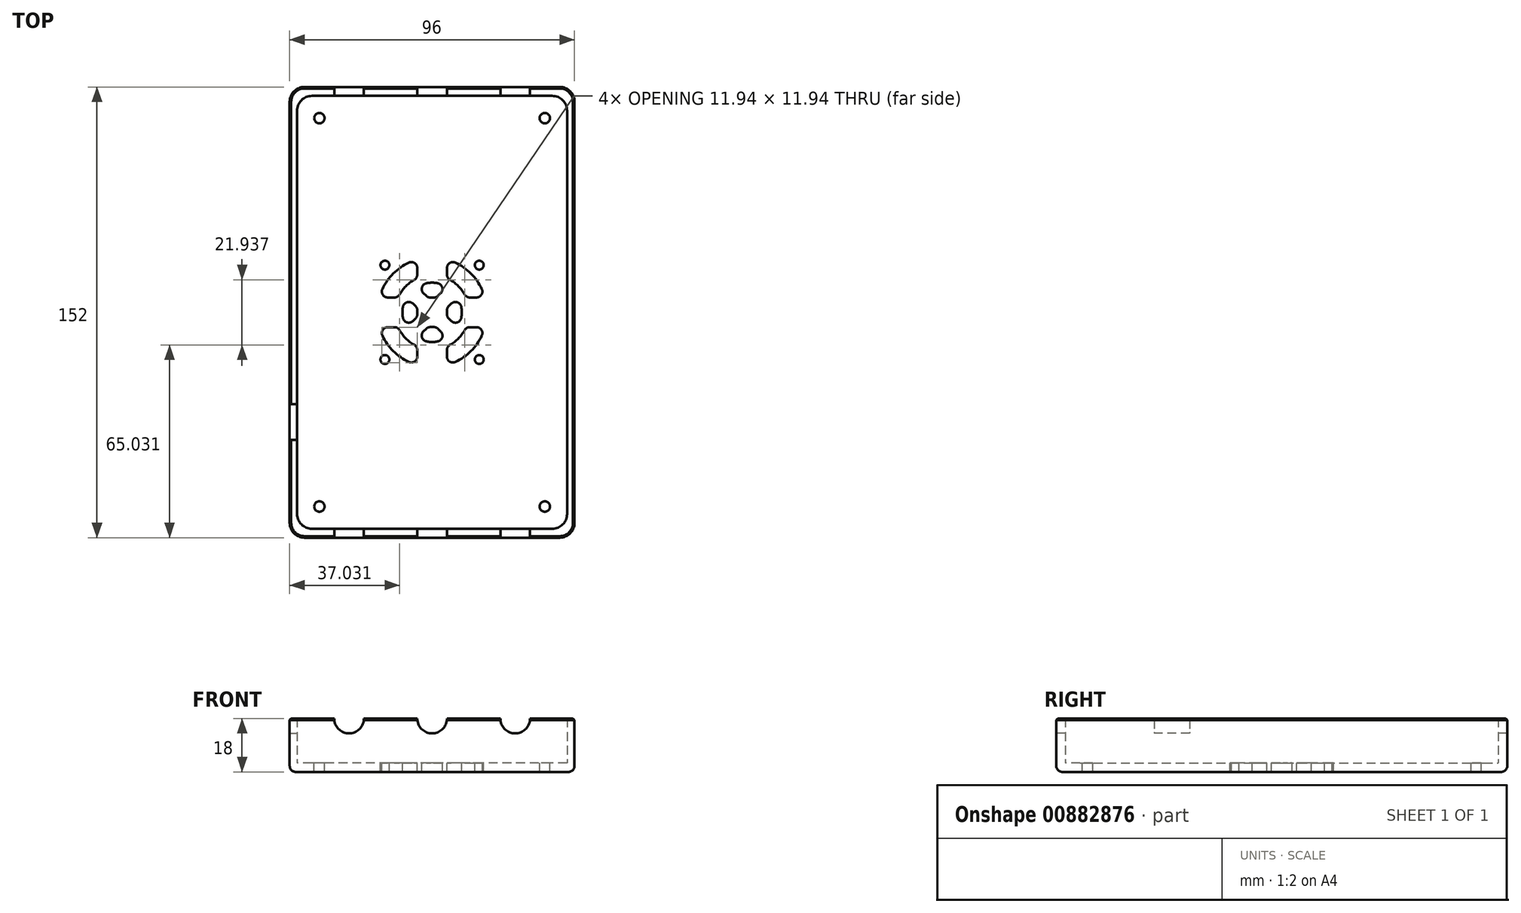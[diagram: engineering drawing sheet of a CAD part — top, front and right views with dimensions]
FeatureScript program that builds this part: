
annotation { "Feature Type Name" : "Feature", "Feature Type Description" : "" }
export const myFeature = defineFeature(function(context is Context, id is Id, definition is map)
    precondition{}
    {
        {
            var Q0;
            Q0=qCreatedBy(makeId("Top.planeOp"),FACE);
            var sketch = newSketch(context, id + "F0", { "sketchPlane" : qUnion([Q0])});
            skLineSegment(sketch, "E0.bottom", {"start": v(48, -76) * mm, "end": v(-48, -76) * mm});
            skLineSegment(sketch, "E0.top", {"start": v(48, 76) * mm, "end": v(-48, 76) * mm});
            skLineSegment(sketch, "E0.left", {"start": v(48, -76) * mm, "end": v(48, 76) * mm});
            skLineSegment(sketch, "E0.right", {"start": v(-48, -76) * mm, "end": v(-48, 76) * mm});
            skPoint(sketch, "E0.middle", {"position": v(0, 0) * mm});
            skSolve(sketch);
        }
        {
            var Q0;
            Q0=qSketchRegion(id+"F0",true);
            extrude(context, id + "F1", {"entities" : qUnion([Q0]), "depth" : 3 * mm, "offsetDistance" : 25 * mm});
        }
        {
            var Q0;
            Q0=makeQuery(id+"F1.opExtrude","CAP_FACE",FACE,{"disambiguationData":[OSD([sQuery(id+"F0.wireOp",EDGE,"E0.bottom"),sQuery(id+"F0.wireOp",EDGE,"E0.top"),sQuery(id+"F0.wireOp",EDGE,"E0.left"),sQuery(id+"F0.wireOp",EDGE,"E0.right")])],"isStart":false});
            var sketch = newSketch(context, id + "F2", { "sketchPlane" : qUnion([Q0])});
            skLineSegment(sketch, "E1.bottom", {"start": v(48, -76) * mm, "end": v(-48, -76) * mm});
            skLineSegment(sketch, "E1.top", {"start": v(48, 76) * mm, "end": v(-48, 76) * mm});
            skLineSegment(sketch, "E1.left", {"start": v(48, -76) * mm, "end": v(48, 76) * mm});
            skLineSegment(sketch, "E1.right", {"start": v(-48, -76) * mm, "end": v(-48, 76) * mm});
            skPoint(sketch, "E1.middle", {"position": v(0, 0) * mm});
            skLineSegment(sketch, "E2.bottom", {"start": v(45.5, -73) * mm, "end": v(-45.5, -73) * mm});
            skLineSegment(sketch, "E2.top", {"start": v(45.5, 73) * mm, "end": v(-45.5, 73) * mm});
            skLineSegment(sketch, "E2.left", {"start": v(45.5, -73) * mm, "end": v(45.5, 73) * mm});
            skLineSegment(sketch, "E2.right", {"start": v(-45.5, -73) * mm, "end": v(-45.5, 73) * mm});
            skSolve(sketch);
        }
        {
            var Q0;
            Q0=qSketchRegion(id+"F2",true);
            extrude(context, id + "F3", {"entities" : qUnion([Q0]), "operationType" : NewBodyOperationType.ADD, "depth" : 15 * mm, "offsetDistance" : 25 * mm});
        }
        {
            var Q0;
            Q0=makeQuery(id+"F1.opExtrude","CAP_FACE",FACE,{"disambiguationData":[OSD([sQuery(id+"F0.wireOp",EDGE,"E0.bottom"),sQuery(id+"F0.wireOp",EDGE,"E0.top"),sQuery(id+"F0.wireOp",EDGE,"E0.left"),sQuery(id+"F0.wireOp",EDGE,"E0.right")])],"isStart":false});
            var sketch = newSketch(context, id + "F4", { "sketchPlane" : qUnion([Q0])});
            skCircle(sketch, "E3", {"center": v(-38, 65.5) * mm, "radius": 1.75 * mm});
            skCircle(sketch, "E4.MirrorC", {"center": v(38, 65.5) * mm, "radius": 1.75 * mm});
            skCircle(sketch, "E5.MirrorC", {"center": v(-38, -65.5) * mm, "radius": 1.75 * mm});
            skCircle(sketch, "E6.MirrorC", {"center": v(38, -65.5) * mm, "radius": 1.75 * mm});
            skSolve(sketch);
        }
        {
            var Q0;
            Q0=qSketchRegion(id+"F4",true);
            extrude(context, id + "F5", {"entities" : qUnion([Q0]), "operationType" : NewBodyOperationType.REMOVE, "endBound" : BoundingType.UP_TO_NEXT, "oppositeDirection" : true, "depth" : 25 * mm, "offsetDistance" : 25 * mm});
        }
        {
            var Q0;
            Q0=makeQuery(id+"F3.boolean.opBoolean","MERGE",EDGE,{"derivedFrom":[makeQuery(id+"F1.opExtrude","SWEPT_EDGE",EDGE,{"disambiguationData":[OSD([sQuery(id+"F0.wireOp",EDGE,"E0.bottom"),sQuery(id+"F0.wireOp",EDGE,"E0.right")])]}),makeQuery(id+"F3.opExtrude","SWEPT_EDGE",EDGE,{"disambiguationData":[OSD([sQuery(id+"F2.wireOp",EDGE,"E1.bottom"),sQuery(id+"F2.wireOp",EDGE,"E1.right")])]})]});
            var Q1;
            Q1=makeQuery(id+"F3.boolean.opBoolean","MERGE",EDGE,{"derivedFrom":[makeQuery(id+"F1.opExtrude","SWEPT_EDGE",EDGE,{"disambiguationData":[OSD([sQuery(id+"F0.wireOp",EDGE,"E0.bottom"),sQuery(id+"F0.wireOp",EDGE,"E0.left")])]}),makeQuery(id+"F3.opExtrude","SWEPT_EDGE",EDGE,{"disambiguationData":[OSD([sQuery(id+"F2.wireOp",EDGE,"E1.bottom"),sQuery(id+"F2.wireOp",EDGE,"E1.left")])]})]});
            var Q2;
            Q2=makeQuery(id+"F3.opExtrude","SWEPT_EDGE",EDGE,{"disambiguationData":[OSD([sQuery(id+"F2.wireOp",EDGE,"E2.bottom"),sQuery(id+"F2.wireOp",EDGE,"E2.left")])]});
            var Q3;
            Q3=makeQuery(id+"F3.opExtrude","SWEPT_EDGE",EDGE,{"disambiguationData":[OSD([sQuery(id+"F2.wireOp",EDGE,"E2.bottom"),sQuery(id+"F2.wireOp",EDGE,"E2.right")])]});
            var Q4;
            Q4=makeQuery(id+"F3.boolean.opBoolean","MERGE",EDGE,{"derivedFrom":[makeQuery(id+"F1.opExtrude","SWEPT_EDGE",EDGE,{"disambiguationData":[OSD([sQuery(id+"F0.wireOp",EDGE,"E0.top"),sQuery(id+"F0.wireOp",EDGE,"E0.right")])]}),makeQuery(id+"F3.opExtrude","SWEPT_EDGE",EDGE,{"disambiguationData":[OSD([sQuery(id+"F2.wireOp",EDGE,"E1.top"),sQuery(id+"F2.wireOp",EDGE,"E1.right")])]})]});
            var Q5;
            Q5=makeQuery(id+"F3.opExtrude","SWEPT_EDGE",EDGE,{"disambiguationData":[OSD([sQuery(id+"F2.wireOp",EDGE,"E2.top"),sQuery(id+"F2.wireOp",EDGE,"E2.right")])]});
            var Q6;
            Q6=makeQuery(id+"F3.boolean.opBoolean","MERGE",EDGE,{"derivedFrom":[makeQuery(id+"F1.opExtrude","SWEPT_EDGE",EDGE,{"disambiguationData":[OSD([sQuery(id+"F0.wireOp",EDGE,"E0.top"),sQuery(id+"F0.wireOp",EDGE,"E0.left")])]}),makeQuery(id+"F3.opExtrude","SWEPT_EDGE",EDGE,{"disambiguationData":[OSD([sQuery(id+"F2.wireOp",EDGE,"E1.top"),sQuery(id+"F2.wireOp",EDGE,"E1.left")])]})]});
            var Q7;
            Q7=makeQuery(id+"F3.opExtrude","SWEPT_EDGE",EDGE,{"disambiguationData":[OSD([sQuery(id+"F2.wireOp",EDGE,"E2.top"),sQuery(id+"F2.wireOp",EDGE,"E2.left")])]});
            fillet(context, id + "F6", {"entities" : qUnion([Q0, Q1, Q2, Q3, Q4, Q5, Q6, Q7]), "radius" : 5 * mm, "tangentPropagation" : true, "allowEdgeOverflow" : false});
        }
        {
            var Q0;
            Q0=makeQuery(id+"F1.opExtrude","CAP_EDGE",EDGE,{"disambiguationData":[OSD([sQuery(id+"F0.wireOp",EDGE,"E0.right")])],"isStart":true});
            fillet(context, id + "F7", {"entities" : qUnion([Q0]), "radius" : 2 * mm, "tangentPropagation" : true, "allowEdgeOverflow" : false});
        }
        {
            var Q0;
            Q0=makeQuery(id+"F3.boolean.opBoolean","MERGE",FACE,{"derivedFrom":[makeQuery(id+"F1.opExtrude","SWEPT_FACE",FACE,{"disambiguationData":[OSD([sQuery(id+"F0.wireOp",EDGE,"E0.bottom")])]}),makeQuery(id+"F3.opExtrude","SWEPT_FACE",FACE,{"disambiguationData":[OSD([sQuery(id+"F2.wireOp",EDGE,"E1.bottom")])]})]});
            var sketch = newSketch(context, id + "F8", { "sketchPlane" : qUnion([Q0])});
            skCircle(sketch, "E7", {"center": v(-28, 18) * mm, "radius": 5 * mm});
            skCircle(sketch, "E8", {"center": v(0, 18) * mm, "radius": 5 * mm});
            skCircle(sketch, "E9", {"center": v(28, 18) * mm, "radius": 5 * mm});
            skSolve(sketch);
        }
        {
            var Q0;
            Q0=qSketchRegion(id+"F8",true);
            extrude(context, id + "F9", {"entities" : qUnion([Q0]), "operationType" : NewBodyOperationType.REMOVE, "endBound" : BoundingType.THROUGH_ALL, "oppositeDirection" : true, "depth" : 25 * mm, "offsetDistance" : 25 * mm});
        }
        {
            var Q0;
            Q0=makeQuery(id+"F3.opExtrude","SWEPT_FACE",FACE,{"disambiguationData":[OSD([sQuery(id+"F2.wireOp",EDGE,"E2.left")])]});
            var sketch = newSketch(context, id + "F10", { "sketchPlane" : qUnion([Q0])});
            skLineSegment(sketch, "E10.bottom", {"start": v(43, 13) * mm, "end": v(31, 13) * mm});
            skLineSegment(sketch, "E10.top", {"start": v(43, 33.9) * mm, "end": v(31, 33.9) * mm});
            skLineSegment(sketch, "E10.left", {"start": v(43, 13) * mm, "end": v(43, 33.9) * mm});
            skLineSegment(sketch, "E10.right", {"start": v(31, 13) * mm, "end": v(31, 33.9) * mm});
            skSolve(sketch);
        }
        {
            var Q0;
            Q0=qSketchRegion(id+"F10",true);
            extrude(context, id + "F11", {"entities" : qUnion([Q0]), "operationType" : NewBodyOperationType.REMOVE, "endBound" : BoundingType.THROUGH_ALL, "depth" : 25 * mm, "offsetDistance" : 25 * mm});
        }
        {
            var Q0;
            Q0=makeQuery(id+"F1.opExtrude","CAP_FACE",FACE,{"disambiguationData":[OSD([sQuery(id+"F0.wireOp",EDGE,"E0.bottom"),sQuery(id+"F0.wireOp",EDGE,"E0.top"),sQuery(id+"F0.wireOp",EDGE,"E0.left"),sQuery(id+"F0.wireOp",EDGE,"E0.right")])],"isStart":false});
            var sketch = newSketch(context, id + "F12", { "sketchPlane" : qUnion([Q0])});
            skLineSegment(sketch, "E11", {"start": v(-18.16, -18.16) * mm, "end": v(29.37, 29.37) * mm, "construction": true});
            skLineSegment(sketch, "E12", {"start": v(19.53, -19.53) * mm, "end": v(-26.87, 26.87) * mm, "construction": true});
            skCircle(sketch, "E13", {"center": v(-15.9, -15.9) * mm, "radius": 1.5 * mm});
            skCircle(sketch, "E14.1.0", {"center": v(15.9, -15.9) * mm, "radius": 1.5 * mm});
            skCircle(sketch, "E14.2.0", {"center": v(15.9, 15.9) * mm, "radius": 1.5 * mm});
            skCircle(sketch, "E14.3.0", {"center": v(-15.9, 15.9) * mm, "radius": 1.5 * mm});
            skPoint(sketch, "E14.center", {"position": v(0, 0) * mm});
            skArc(sketch, "E15", {"start": v(16.75, 7.85) * mm, "mid": v(13.08, 13.08) * mm, "end": v(7.85, 16.75) * mm});
            skArc(sketch, "E16", {"start": v(10.95, 6.03) * mm, "mid": v(8.84, 8.84) * mm, "end": v(6.03, 10.95) * mm});
            skLineSegment(sketch, "E17", {"start": v(12.7, 5) * mm, "end": v(14.94, 5) * mm});
            skLineSegment(sketch, "E18.MirrorCS", {"start": v(12.7, -5) * mm, "end": v(14.94, -5) * mm});
            skPoint(sketch, "E19.orphan", {"position": v(28.67, -5) * mm});
            skPoint(sketch, "E20.orphan", {"position": v(8.36, 5) * mm});
            skPoint(sketch, "E21.orphan", {"position": v(8.36, -5) * mm});
            skPoint(sketch, "E22.orphan", {"position": v(28.67, 5) * mm});
            skPoint(sketch, "E23.visualSharp", {"position": v(11.46, -5) * mm});
            skArc(sketch, "E23.filletArc", {"start": v(12.7, -5) * mm, "mid": v(11.68, -5.28) * mm, "end": v(10.95, -6.03) * mm});
            skPoint(sketch, "E24.visualSharp", {"position": v(17.81, -5) * mm});
            skArc(sketch, "E24.filletArc", {"start": v(16.75, -7.85) * mm, "mid": v(16.63, -5.93) * mm, "end": v(14.94, -5) * mm});
            skPoint(sketch, "E25.visualSharp", {"position": v(11.46, 5) * mm});
            skArc(sketch, "E25.filletArc", {"start": v(10.95, 6.03) * mm, "mid": v(11.68, 5.28) * mm, "end": v(12.7, 5) * mm});
            skPoint(sketch, "E26.visualSharp", {"position": v(17.81, 5) * mm});
            skArc(sketch, "E26.filletArc", {"start": v(14.94, 5) * mm, "mid": v(16.63, 5.93) * mm, "end": v(16.75, 7.85) * mm});
            skArc(sketch, "E27.1.0", {"start": v(7.85, 16.75) * mm, "mid": v(5.93, 16.63) * mm, "end": v(5, 14.94) * mm});
            skLineSegment(sketch, "E27.1.1", {"start": v(5, 12.7) * mm, "end": v(5, 14.94) * mm});
            skArc(sketch, "E27.1.2", {"start": v(5, 12.7) * mm, "mid": v(5.28, 11.68) * mm, "end": v(6.03, 10.95) * mm});
            skArc(sketch, "E27.1.3", {"start": v(-6.03, 10.95) * mm, "mid": v(-5.28, 11.68) * mm, "end": v(-5, 12.7) * mm});
            skLineSegment(sketch, "E27.1.4", {"start": v(-5, 12.7) * mm, "end": v(-5, 14.94) * mm});
            skArc(sketch, "E27.1.5", {"start": v(-5, 14.94) * mm, "mid": v(-5.93, 16.63) * mm, "end": v(-7.85, 16.75) * mm});
            skArc(sketch, "E27.2.0", {"start": v(-16.75, 7.85) * mm, "mid": v(-16.63, 5.93) * mm, "end": v(-14.94, 5) * mm});
            skLineSegment(sketch, "E27.2.1", {"start": v(-12.7, 5) * mm, "end": v(-14.94, 5) * mm});
            skArc(sketch, "E27.2.2", {"start": v(-12.7, 5) * mm, "mid": v(-11.68, 5.28) * mm, "end": v(-10.95, 6.03) * mm});
            skArc(sketch, "E27.2.3", {"start": v(-10.95, -6.03) * mm, "mid": v(-11.68, -5.28) * mm, "end": v(-12.7, -5) * mm});
            skLineSegment(sketch, "E27.2.4", {"start": v(-12.7, -5) * mm, "end": v(-14.94, -5) * mm});
            skArc(sketch, "E27.2.5", {"start": v(-14.94, -5) * mm, "mid": v(-16.63, -5.93) * mm, "end": v(-16.75, -7.85) * mm});
            skArc(sketch, "E27.3.0", {"start": v(-7.85, -16.75) * mm, "mid": v(-5.93, -16.63) * mm, "end": v(-5, -14.94) * mm});
            skLineSegment(sketch, "E27.3.1", {"start": v(-5, -12.7) * mm, "end": v(-5, -14.94) * mm});
            skArc(sketch, "E27.3.2", {"start": v(-5, -12.7) * mm, "mid": v(-5.28, -11.68) * mm, "end": v(-6.03, -10.95) * mm});
            skArc(sketch, "E27.3.3", {"start": v(6.03, -10.95) * mm, "mid": v(5.28, -11.68) * mm, "end": v(5, -12.7) * mm});
            skLineSegment(sketch, "E27.3.4", {"start": v(5, -12.7) * mm, "end": v(5, -14.94) * mm});
            skArc(sketch, "E27.3.5", {"start": v(5, -14.94) * mm, "mid": v(5.93, -16.63) * mm, "end": v(7.85, -16.75) * mm});
            skArc(sketch, "E28.trimOffspring", {"start": v(-7.85, 16.75) * mm, "mid": v(-13.08, 13.08) * mm, "end": v(-16.75, 7.85) * mm});
            skArc(sketch, "E29.trimOffspring", {"start": v(-6.03, 10.95) * mm, "mid": v(-8.84, 8.84) * mm, "end": v(-10.95, 6.03) * mm});
            skArc(sketch, "E30.trimOffspring", {"start": v(-10.95, -6.03) * mm, "mid": v(-8.84, -8.84) * mm, "end": v(-6.03, -10.95) * mm});
            skArc(sketch, "E31.trimOffspring", {"start": v(-16.75, -7.85) * mm, "mid": v(-13.08, -13.08) * mm, "end": v(-7.85, -16.75) * mm});
            skArc(sketch, "E32.trimOffspring", {"start": v(6.03, -10.95) * mm, "mid": v(8.84, -8.84) * mm, "end": v(10.95, -6.03) * mm});
            skArc(sketch, "E33.trimOffspring", {"start": v(7.85, -16.75) * mm, "mid": v(13.08, -13.08) * mm, "end": v(16.75, -7.85) * mm});
            skArc(sketch, "E34", {"start": v(9.82, -1.87) * mm, "mid": v(10, 0) * mm, "end": v(9.82, 1.87) * mm});
            skArc(sketch, "E35", {"start": v(4.98, -0.44) * mm, "mid": v(5, 0) * mm, "end": v(4.98, 0.44) * mm});
            skLineSegment(sketch, "E36", {"start": v(2.02, -5.56) * mm, "end": v(2.9, -6.44) * mm});
            skLineSegment(sketch, "E37.MirrorCS", {"start": v(5.56, -2.02) * mm, "end": v(6.44, -2.9) * mm});
            skPoint(sketch, "E38.orphan", {"position": v(9.7, -6.17) * mm});
            skPoint(sketch, "E39.orphan", {"position": v(6.17, -9.7) * mm});
            skPoint(sketch, "E40.orphan", {"position": v(0.7, -4.24) * mm});
            skPoint(sketch, "E41.orphan", {"position": v(4.24, -0.7) * mm});
            skPoint(sketch, "E42.visualSharp", {"position": v(1.3, -4.83) * mm});
            skArc(sketch, "E42.filletArc", {"start": v(2.02, -5.56) * mm, "mid": v(1.3, -5.1) * mm, "end": v(0.44, -4.98) * mm});
            skPoint(sketch, "E43.visualSharp", {"position": v(5.08, -8.61) * mm});
            skArc(sketch, "E43.filletArc", {"start": v(1.87, -9.82) * mm, "mid": v(3.4, -8.45) * mm, "end": v(2.9, -6.44) * mm});
            skPoint(sketch, "E44.visualSharp", {"position": v(4.83, -1.3) * mm});
            skArc(sketch, "E44.filletArc", {"start": v(4.98, -0.44) * mm, "mid": v(5.1, -1.3) * mm, "end": v(5.56, -2.02) * mm});
            skPoint(sketch, "E45.visualSharp", {"position": v(8.61, -5.08) * mm});
            skArc(sketch, "E45.filletArc", {"start": v(6.44, -2.9) * mm, "mid": v(8.45, -3.4) * mm, "end": v(9.82, -1.87) * mm});
            skArc(sketch, "E46.1.0", {"start": v(5.56, 2.02) * mm, "mid": v(5.1, 1.3) * mm, "end": v(4.98, 0.44) * mm});
            skLineSegment(sketch, "E46.1.1", {"start": v(5.56, 2.02) * mm, "end": v(6.44, 2.9) * mm});
            skArc(sketch, "E46.1.2", {"start": v(9.82, 1.87) * mm, "mid": v(8.45, 3.4) * mm, "end": v(6.44, 2.9) * mm});
            skArc(sketch, "E46.1.3", {"start": v(0.44, 4.98) * mm, "mid": v(1.3, 5.1) * mm, "end": v(2.02, 5.56) * mm});
            skLineSegment(sketch, "E46.1.4", {"start": v(2.02, 5.56) * mm, "end": v(2.9, 6.44) * mm});
            skArc(sketch, "E46.1.5", {"start": v(2.9, 6.44) * mm, "mid": v(3.4, 8.45) * mm, "end": v(1.87, 9.82) * mm});
            skArc(sketch, "E46.2.0", {"start": v(-2.02, 5.56) * mm, "mid": v(-1.3, 5.1) * mm, "end": v(-0.44, 4.98) * mm});
            skLineSegment(sketch, "E46.2.1", {"start": v(-2.02, 5.56) * mm, "end": v(-2.9, 6.44) * mm});
            skArc(sketch, "E46.2.2", {"start": v(-1.87, 9.82) * mm, "mid": v(-3.4, 8.45) * mm, "end": v(-2.9, 6.44) * mm});
            skArc(sketch, "E46.2.3", {"start": v(-4.98, 0.44) * mm, "mid": v(-5.1, 1.3) * mm, "end": v(-5.56, 2.02) * mm});
            skLineSegment(sketch, "E46.2.4", {"start": v(-5.56, 2.02) * mm, "end": v(-6.44, 2.9) * mm});
            skArc(sketch, "E46.2.5", {"start": v(-6.44, 2.9) * mm, "mid": v(-8.45, 3.4) * mm, "end": v(-9.82, 1.87) * mm});
            skArc(sketch, "E46.3.0", {"start": v(-5.56, -2.02) * mm, "mid": v(-5.1, -1.3) * mm, "end": v(-4.98, -0.44) * mm});
            skLineSegment(sketch, "E46.3.1", {"start": v(-5.56, -2.02) * mm, "end": v(-6.44, -2.9) * mm});
            skArc(sketch, "E46.3.2", {"start": v(-9.82, -1.87) * mm, "mid": v(-8.45, -3.4) * mm, "end": v(-6.44, -2.9) * mm});
            skArc(sketch, "E46.3.3", {"start": v(-0.44, -4.98) * mm, "mid": v(-1.3, -5.1) * mm, "end": v(-2.02, -5.56) * mm});
            skLineSegment(sketch, "E46.3.4", {"start": v(-2.02, -5.56) * mm, "end": v(-2.9, -6.44) * mm});
            skArc(sketch, "E46.3.5", {"start": v(-2.9, -6.44) * mm, "mid": v(-3.4, -8.45) * mm, "end": v(-1.87, -9.82) * mm});
            skArc(sketch, "E47.trimOffspring", {"start": v(0.44, 4.98) * mm, "mid": v(0, 5) * mm, "end": v(-0.44, 4.98) * mm});
            skArc(sketch, "E48.trimOffspring", {"start": v(-4.98, 0.44) * mm, "mid": v(-5, 0) * mm, "end": v(-4.98, -0.44) * mm});
            skArc(sketch, "E49.trimOffspring", {"start": v(-0.44, -4.98) * mm, "mid": v(0, -5) * mm, "end": v(0.44, -4.98) * mm});
            skArc(sketch, "E50.trimOffspring", {"start": v(1.87, 9.82) * mm, "mid": v(0, 10) * mm, "end": v(-1.87, 9.82) * mm});
            skArc(sketch, "E51.trimOffspring", {"start": v(-9.82, 1.87) * mm, "mid": v(-10, 0) * mm, "end": v(-9.82, -1.87) * mm});
            skArc(sketch, "E52.trimOffspring", {"start": v(-1.87, -9.82) * mm, "mid": v(0, -10) * mm, "end": v(1.87, -9.82) * mm});
            skSolve(sketch);
        }
        {
            var Q0;
            Q0 = qSketchRegion(id + "F12", true);
            extrude(context, id + "F13", {"entities" : qUnion([Q0]), "operationType" : NewBodyOperationType.REMOVE, "endBound" : BoundingType.UP_TO_NEXT, "oppositeDirection" : true, "depth" : 25 * mm, "offsetDistance" : 25 * mm});
        }
        {
            var Q0;
            Q0=makeQuery(id+"F3.opExtrude","CAP_EDGE",EDGE,{"disambiguationData":[OSD([sQuery(id+"F2.wireOp",EDGE,"E1.left")])],"isStart":false});
            var Q1;
            {var subQ0=sQuery(id+"F2.wireOp",EDGE,"E1.top");Q1=makeQuery(id+"F9.boolean.opBoolean","SPLIT",EDGE,{"disambiguationData":[TD([makeQuery(id+"F1.opExtrude","SWEPT_FACE",FACE,{"disambiguationData":[OSD([sQuery(id+"F0.wireOp",EDGE,"E0.top")])]}),makeQuery(id+"F3.opExtrude","CAP_FACE",FACE,{"disambiguationData":[OSD([sQuery(id+"F2.wireOp",EDGE,"E1.bottom"),subQ0,sQuery(id+"F2.wireOp",EDGE,"E1.left"),sQuery(id+"F2.wireOp",EDGE,"E1.right"),sQuery(id+"F2.wireOp",EDGE,"E2.bottom"),sQuery(id+"F2.wireOp",EDGE,"E2.top"),sQuery(id+"F2.wireOp",EDGE,"E2.left"),sQuery(id+"F2.wireOp",EDGE,"E2.right")])],"isStart":false}),makeQuery(id+"F3.opExtrude","SWEPT_FACE",FACE,{"disambiguationData":[OSD([subQ0])]}),makeQuery(id+"F9.opExtrude","SWEPT_FACE",FACE,{"disambiguationData":[OSD([sQuery(id+"F8.wireOp",EDGE,"E8")])]}),makeQuery(id+"F9.opExtrude","SWEPT_FACE",FACE,{"disambiguationData":[OSD([sQuery(id+"F8.wireOp",EDGE,"E9")])]})])],"derivedFrom":makeQuery(id+"F3.opExtrude","CAP_EDGE",EDGE,{"disambiguationData":[OSD([subQ0])],"isStart":false})});}
            var Q2;
            {var subQ0=sQuery(id+"F2.wireOp",EDGE,"E1.top");Q2=makeQuery(id+"F9.boolean.opBoolean","SPLIT",EDGE,{"disambiguationData":[TD([makeQuery(id+"F1.opExtrude","SWEPT_FACE",FACE,{"disambiguationData":[OSD([sQuery(id+"F0.wireOp",EDGE,"E0.top")])]}),makeQuery(id+"F3.opExtrude","CAP_FACE",FACE,{"disambiguationData":[OSD([sQuery(id+"F2.wireOp",EDGE,"E1.bottom"),subQ0,sQuery(id+"F2.wireOp",EDGE,"E1.left"),sQuery(id+"F2.wireOp",EDGE,"E1.right"),sQuery(id+"F2.wireOp",EDGE,"E2.bottom"),sQuery(id+"F2.wireOp",EDGE,"E2.top"),sQuery(id+"F2.wireOp",EDGE,"E2.left"),sQuery(id+"F2.wireOp",EDGE,"E2.right")])],"isStart":false}),makeQuery(id+"F3.opExtrude","SWEPT_FACE",FACE,{"disambiguationData":[OSD([subQ0])]}),makeQuery(id+"F9.opExtrude","SWEPT_FACE",FACE,{"disambiguationData":[OSD([sQuery(id+"F8.wireOp",EDGE,"E7")])]}),makeQuery(id+"F9.opExtrude","SWEPT_FACE",FACE,{"disambiguationData":[OSD([sQuery(id+"F8.wireOp",EDGE,"E8")])]})])],"derivedFrom":makeQuery(id+"F3.opExtrude","CAP_EDGE",EDGE,{"disambiguationData":[OSD([subQ0])],"isStart":false})});}
            var Q3;
            {var subQ0=sQuery(id+"F2.wireOp",EDGE,"E1.right");var subQ1=sQuery(id+"F2.wireOp",EDGE,"E1.top");var subQ2=sQuery(id+"F0.wireOp",EDGE,"E0.top");Q3=makeQuery(id+"F9.boolean.opBoolean","SPLIT",EDGE,{"disambiguationData":[TD([makeQuery(id+"F1.opExtrude","SWEPT_FACE",FACE,{"disambiguationData":[OSD([subQ2])]}),makeQuery(id+"F3.opExtrude","CAP_FACE",FACE,{"disambiguationData":[OSD([sQuery(id+"F2.wireOp",EDGE,"E1.bottom"),subQ1,sQuery(id+"F2.wireOp",EDGE,"E1.left"),subQ0,sQuery(id+"F2.wireOp",EDGE,"E2.bottom"),sQuery(id+"F2.wireOp",EDGE,"E2.top"),sQuery(id+"F2.wireOp",EDGE,"E2.left"),sQuery(id+"F2.wireOp",EDGE,"E2.right")])],"isStart":false}),makeQuery(id+"F3.opExtrude","SWEPT_FACE",FACE,{"disambiguationData":[OSD([subQ1])]}),makeQuery(id+"F6.opFillet","BLEND_FACE",FACE,{"disambiguationData":[OSD([subQ2,sQuery(id+"F0.wireOp",EDGE,"E0.right"),subQ1,subQ0])]}),makeQuery(id+"F9.opExtrude","SWEPT_FACE",FACE,{"disambiguationData":[OSD([sQuery(id+"F8.wireOp",EDGE,"E7")])]})])],"derivedFrom":makeQuery(id+"F3.opExtrude","CAP_EDGE",EDGE,{"disambiguationData":[OSD([subQ1])],"isStart":false})});}
            var Q4;
            {var subQ0=sQuery(id+"F2.wireOp",EDGE,"E1.right");Q4=makeQuery(id+"F11.boolean.opBoolean","SPLIT",EDGE,{"disambiguationData":[TD([makeQuery(id+"F11.opExtrude","SWEPT_FACE",FACE,{"disambiguationData":[OSD([sQuery(id+"F10.wireOp",EDGE,"E10.left")])]})])],"derivedFrom":makeQuery(id+"F3.opExtrude","CAP_EDGE",EDGE,{"disambiguationData":[OSD([subQ0])],"isStart":false})});}
            var Q5;
            {var subQ0=sQuery(id+"F2.wireOp",EDGE,"E1.bottom");Q5=makeQuery(id+"F9.boolean.opBoolean","SPLIT",EDGE,{"disambiguationData":[TD([makeQuery(id+"F1.opExtrude","SWEPT_FACE",FACE,{"disambiguationData":[OSD([sQuery(id+"F0.wireOp",EDGE,"E0.bottom")])]}),makeQuery(id+"F3.opExtrude","SWEPT_FACE",FACE,{"disambiguationData":[OSD([subQ0])]}),makeQuery(id+"F3.opExtrude","CAP_FACE",FACE,{"disambiguationData":[OSD([subQ0,sQuery(id+"F2.wireOp",EDGE,"E1.top"),sQuery(id+"F2.wireOp",EDGE,"E1.left"),sQuery(id+"F2.wireOp",EDGE,"E1.right"),sQuery(id+"F2.wireOp",EDGE,"E2.bottom"),sQuery(id+"F2.wireOp",EDGE,"E2.top"),sQuery(id+"F2.wireOp",EDGE,"E2.left"),sQuery(id+"F2.wireOp",EDGE,"E2.right")])],"isStart":false}),makeQuery(id+"F9.opExtrude","SWEPT_FACE",FACE,{"disambiguationData":[OSD([sQuery(id+"F8.wireOp",EDGE,"E7")])]}),makeQuery(id+"F9.opExtrude","SWEPT_FACE",FACE,{"disambiguationData":[OSD([sQuery(id+"F8.wireOp",EDGE,"E8")])]})])],"derivedFrom":makeQuery(id+"F3.opExtrude","CAP_EDGE",EDGE,{"disambiguationData":[OSD([subQ0])],"isStart":false})});}
            var Q6;
            {var subQ0=sQuery(id+"F2.wireOp",EDGE,"E1.bottom");Q6=makeQuery(id+"F9.boolean.opBoolean","SPLIT",EDGE,{"disambiguationData":[TD([makeQuery(id+"F1.opExtrude","SWEPT_FACE",FACE,{"disambiguationData":[OSD([sQuery(id+"F0.wireOp",EDGE,"E0.bottom")])]}),makeQuery(id+"F3.opExtrude","SWEPT_FACE",FACE,{"disambiguationData":[OSD([subQ0])]}),makeQuery(id+"F3.opExtrude","CAP_FACE",FACE,{"disambiguationData":[OSD([subQ0,sQuery(id+"F2.wireOp",EDGE,"E1.top"),sQuery(id+"F2.wireOp",EDGE,"E1.left"),sQuery(id+"F2.wireOp",EDGE,"E1.right"),sQuery(id+"F2.wireOp",EDGE,"E2.bottom"),sQuery(id+"F2.wireOp",EDGE,"E2.top"),sQuery(id+"F2.wireOp",EDGE,"E2.left"),sQuery(id+"F2.wireOp",EDGE,"E2.right")])],"isStart":false}),makeQuery(id+"F9.opExtrude","SWEPT_FACE",FACE,{"disambiguationData":[OSD([sQuery(id+"F8.wireOp",EDGE,"E8")])]}),makeQuery(id+"F9.opExtrude","SWEPT_FACE",FACE,{"disambiguationData":[OSD([sQuery(id+"F8.wireOp",EDGE,"E9")])]})])],"derivedFrom":makeQuery(id+"F3.opExtrude","CAP_EDGE",EDGE,{"disambiguationData":[OSD([subQ0])],"isStart":false})});}
            chamfer(context, id + "F14", {"entities" : qUnion([Q0, Q1, Q2, Q3, Q4, Q5, Q6]), "width" : .5 * mm, "tangentPropagation" : true});
        }
    });
